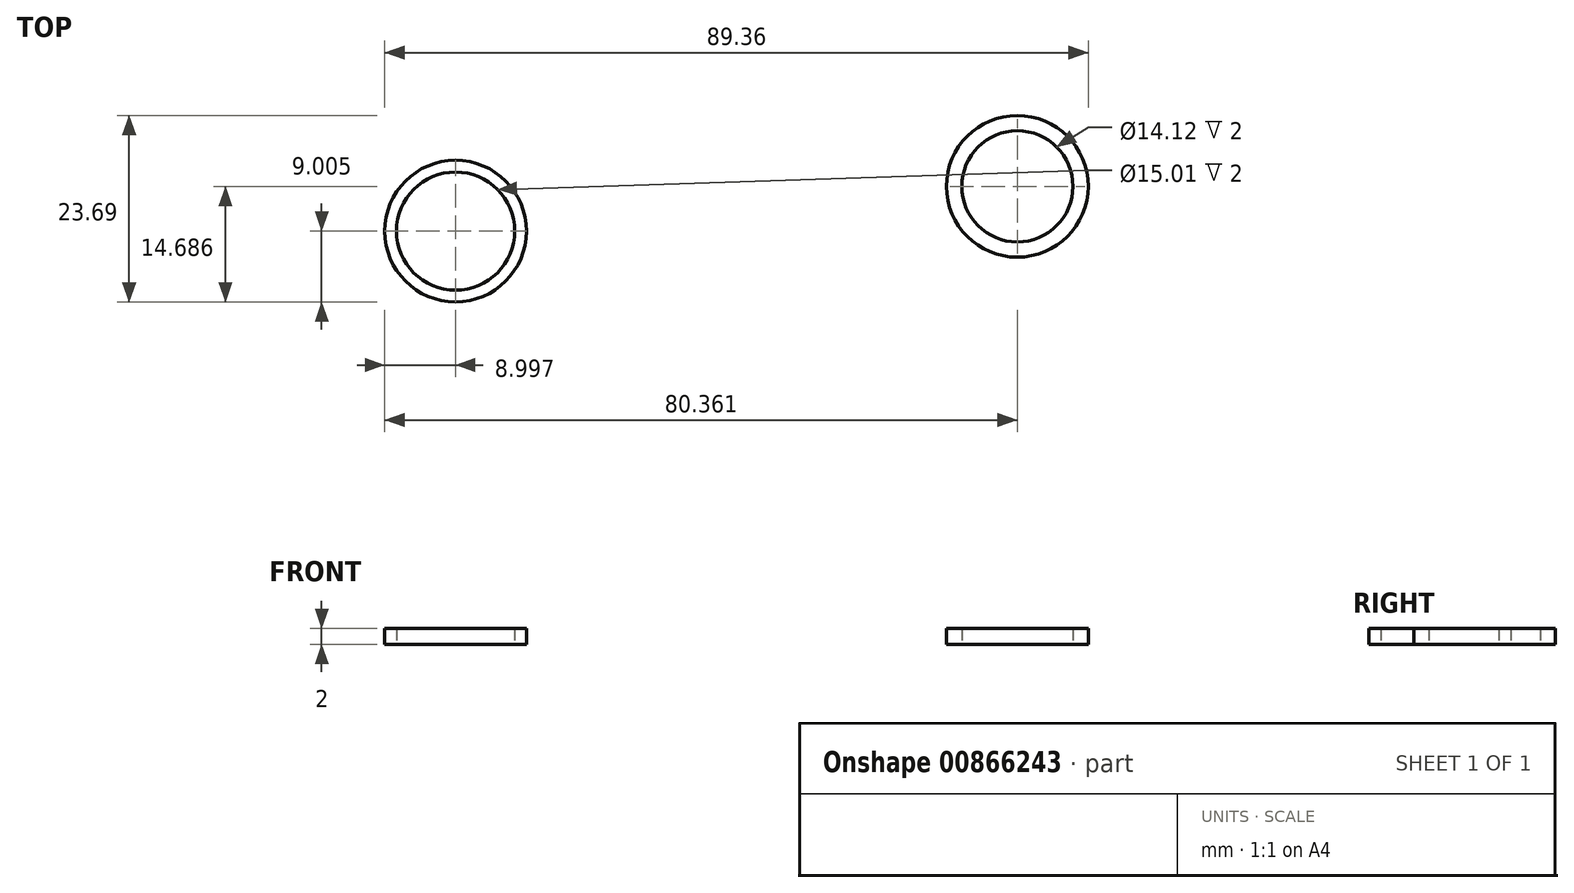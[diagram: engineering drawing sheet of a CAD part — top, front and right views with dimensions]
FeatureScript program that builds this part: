
annotation { "Feature Type Name" : "Feature", "Feature Type Description" : "" }
export const myFeature = defineFeature(function(context is Context, id is Id, definition is map)
    precondition{}
    {
        {
            var Q0;
            Q0=qCreatedBy(makeId("Top.planeOp"),FACE);
            var sketch = newSketch(context, id + "F0", { "sketchPlane" : qUnion([Q0])});
            skCircle(sketch, "E0", {"center": v(-23.52, 27.95) * mm, "radius": 7.5 * mm});
            skCircle(sketch, "E1", {"center": v(47.84, 33.64) * mm, "radius": 7.06 * mm});
            skCircle(sketch, "E2", {"center": v(-23.52, 27.95) * mm, "radius": 9 * mm});
            skCircle(sketch, "E3", {"center": v(47.84, 33.64) * mm, "radius": 1 * mm});
            skCircle(sketch, "E4", {"center": v(47.84, 33.64) * mm, "radius": 9 * mm});
            skSolve(sketch);
        }
        {
            var Q0;
            Q0=makeQuery(id+"F0.imprint","IMPRINT",FACE,{"disambiguationData":[TD([[makeQuery(id+"F0.imprint","IMPRINT",EDGE,{"derivedFrom":sQuery(id+"F0.wireOp",EDGE,"E0")}),-1.0]])]});
            extrude(context, id + "F1", {"entities" : qUnion([Q0]), "depth" : 2 * mm, "offsetDistance" : 25 * mm});
        }
        {
            var Q0;
            Q0=makeQuery(id+"F0.imprint","IMPRINT",FACE,{"disambiguationData":[TD([[makeQuery(id+"F0.imprint","IMPRINT",EDGE,{"derivedFrom":sQuery(id+"F0.wireOp",EDGE,"E1")}),-1.0]])]});
            extrude(context, id + "F2", {"entities" : qUnion([Q0]), "depth" : 2 * mm, "offsetDistance" : 25 * mm});
        }
    });
